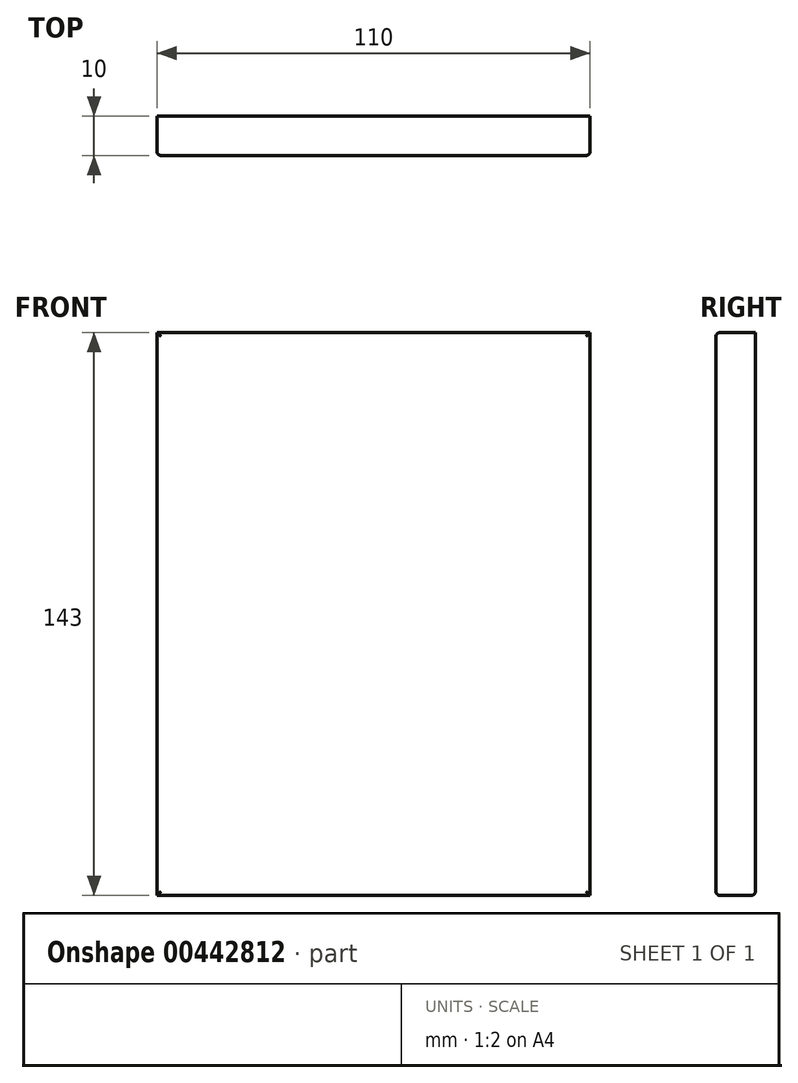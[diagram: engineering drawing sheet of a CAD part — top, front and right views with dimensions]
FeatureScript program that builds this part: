
annotation { "Feature Type Name" : "Feature", "Feature Type Description" : "" }
export const myFeature = defineFeature(function(context is Context, id is Id, definition is map)
    precondition{}
    {
        {
            var Q0;
            Q0=qCreatedBy(makeId("Front.planeOp"),FACE);
            var sketch = newSketch(context, id + "F0", { "sketchPlane" : qUnion([Q0])});
            skLineSegment(sketch, "E0.bottom", {"start": v(0, 0) * mm, "end": v(-110, 0) * mm});
            skLineSegment(sketch, "E0.top", {"start": v(0, 143) * mm, "end": v(-110, 143) * mm});
            skLineSegment(sketch, "E0.left", {"start": v(0, 0) * mm, "end": v(0, 143) * mm});
            skLineSegment(sketch, "E0.right", {"start": v(-110, 0) * mm, "end": v(-110, 143) * mm});
            skSolve(sketch);
        }
        {
            var Q0;
            Q0 = qSketchRegion(id + "F0", true);
            extrude(context, id + "F1", {"entities" : qUnion([Q0]), "depth" : 10 * mm, "offsetDistance" : 25 * mm});
        }
        {
            var Q0;
            Q0=makeQuery(id+"F1.opExtrude","CAP_EDGE",EDGE,{"disambiguationData":[OSD([sQuery(id+"F0.wireOp",EDGE,"E0.left")])],"isStart":false});
            var Q1;
            Q1=makeQuery(id+"F1.opExtrude","CAP_EDGE",EDGE,{"disambiguationData":[OSD([sQuery(id+"F0.wireOp",EDGE,"E0.right")])],"isStart":false});
            var Q2;
            Q2=makeQuery(id+"F1.opExtrude","CAP_EDGE",EDGE,{"disambiguationData":[OSD([sQuery(id+"F0.wireOp",EDGE,"E0.bottom")])],"isStart":true});
            var Q3;
            Q3=makeQuery(id+"F1.opExtrude","CAP_FACE",FACE,{"disambiguationData":[OSD([sQuery(id+"F0.wireOp",EDGE,"E0.bottom"),sQuery(id+"F0.wireOp",EDGE,"E0.top"),sQuery(id+"F0.wireOp",EDGE,"E0.left"),sQuery(id+"F0.wireOp",EDGE,"E0.right")])],"isStart":false});
            fillet(context, id + "F2", {"entities" : qUnion([Q0, Q1, Q2, Q3]), "radius" : 1 * mm, "tangentPropagation" : true, "allowEdgeOverflow" : false});
        }
    });
